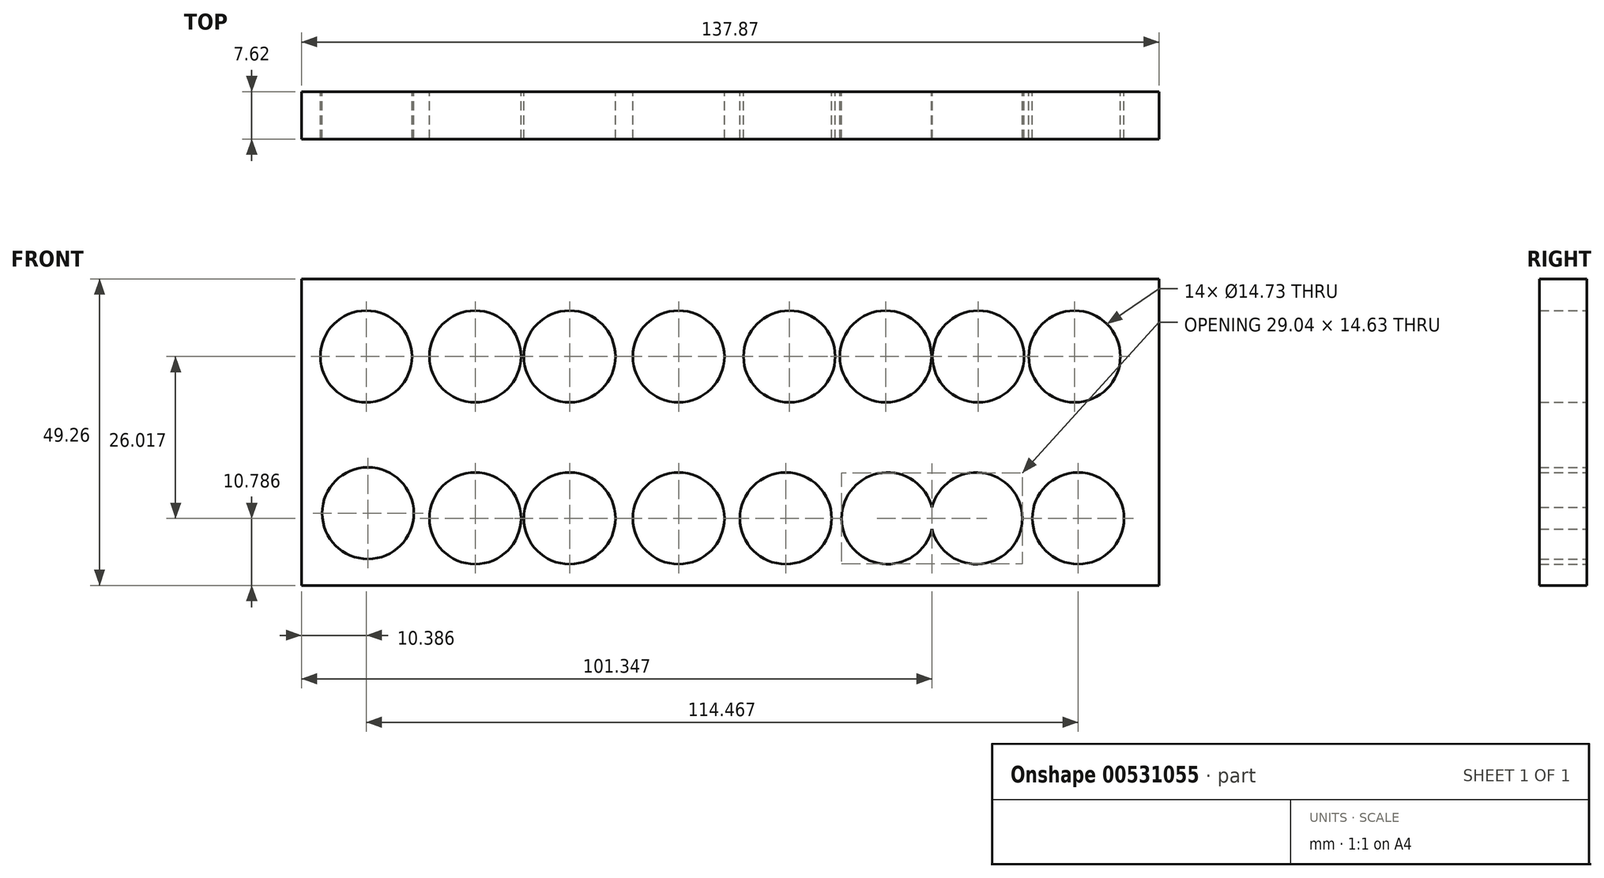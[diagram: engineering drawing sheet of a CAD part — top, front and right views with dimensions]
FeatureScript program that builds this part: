
annotation { "Feature Type Name" : "Feature", "Feature Type Description" : "" }
export const myFeature = defineFeature(function(context is Context, id is Id, definition is map)
    precondition{}
    {
        {
            var Q0;
            Q0=qCreatedBy(makeId("Front.planeOp"),FACE);
            var sketch = newSketch(context, id + "F0", { "sketchPlane" : qUnion([Q0])});
            skLineSegment(sketch, "E0.bottom", {"start": v(-69.08, 21.13) * mm, "end": v(68.79, 21.13) * mm});
            skLineSegment(sketch, "E0.top", {"start": v(-69.08, -28.13) * mm, "end": v(68.79, -28.13) * mm});
            skLineSegment(sketch, "E0.left", {"start": v(-69.08, 21.13) * mm, "end": v(-69.08, -28.13) * mm});
            skLineSegment(sketch, "E0.right", {"start": v(68.79, 21.13) * mm, "end": v(68.79, -28.13) * mm});
            skSolve(sketch);
        }
        {
            var Q0;
            Q0=makeQuery(id+"F0.imprint","IMPRINT",FACE,{"disambiguationData":[TD([[makeQuery(id+"F0.imprint","IMPRINT",EDGE,{"derivedFrom":sQuery(id+"F0.wireOp",EDGE,"E0.bottom")}),-1.0]])]});
            extrude(context, id + "F1", {"entities" : qUnion([Q0]), "depth" : 7.62 * mm, "offsetDistance" : 25.4 * mm});
        }
        {
            var Q0;
            Q0=makeQuery(id+"F1.opExtrude","CAP_FACE",FACE,{"disambiguationData":[OSD([sQuery(id+"F0.wireOp",EDGE,"E0.bottom"),sQuery(id+"F0.wireOp",EDGE,"E0.top"),sQuery(id+"F0.wireOp",EDGE,"E0.left"),sQuery(id+"F0.wireOp",EDGE,"E0.right")])],"isStart":true});
            var sketch = newSketch(context, id + "F2", { "sketchPlane" : qUnion([Q0])});
            skPoint(sketch, "E1", {"position": v(58.4, -16.52) * mm});
            skPoint(sketch, "E2", {"position": v(58.7, 8.67) * mm});
            skPoint(sketch, "E3", {"position": v(41.17, -17.34) * mm});
            skPoint(sketch, "E4", {"position": v(41.17, 8.67) * mm});
            skPoint(sketch, "E5", {"position": v(25.99, -17.34) * mm});
            skPoint(sketch, "E6", {"position": v(25.99, 8.67) * mm});
            skPoint(sketch, "E7", {"position": v(8.47, -17.34) * mm});
            skPoint(sketch, "E8", {"position": v(8.47, 8.67) * mm});
            skPoint(sketch, "E9", {"position": v(-8.76, -17.34) * mm});
            skPoint(sketch, "E10", {"position": v(-9.34, 8.67) * mm});
            skPoint(sketch, "E11", {"position": v(-25.11, -17.34) * mm});
            skPoint(sketch, "E12", {"position": v(-24.82, 8.67) * mm});
            skPoint(sketch, "E13", {"position": v(-39.42, -17.34) * mm});
            skPoint(sketch, "E14", {"position": v(-39.71, 8.67) * mm});
            skPoint(sketch, "E15", {"position": v(-55.77, -17.34) * mm});
            skPoint(sketch, "E16", {"position": v(-55.19, 8.67) * mm});
            skSolve(sketch);
        }
        {
            var Q0;
            Q0=sQuery(id+"F2.wireOp",VERTEX,"E1");
            var Q1;
            Q1=sQuery(id+"F2.wireOp",VERTEX,"E2");
            var Q2;
            Q2=sQuery(id+"F2.wireOp",VERTEX,"E3");
            var Q3;
            Q3=sQuery(id+"F2.wireOp",VERTEX,"E4");
            var Q4;
            Q4=sQuery(id+"F2.wireOp",VERTEX,"E5");
            var Q5;
            Q5=sQuery(id+"F2.wireOp",VERTEX,"E6");
            var Q6;
            Q6=sQuery(id+"F2.wireOp",VERTEX,"E7");
            var Q7;
            Q7=sQuery(id+"F2.wireOp",VERTEX,"E8");
            var Q8;
            Q8=sQuery(id+"F2.wireOp",VERTEX,"E9");
            var Q9;
            Q9=sQuery(id+"F2.wireOp",VERTEX,"E10");
            var Q10;
            Q10=sQuery(id+"F2.wireOp",VERTEX,"E11");
            var Q11;
            Q11=sQuery(id+"F2.wireOp",VERTEX,"E12");
            var Q12;
            Q12=sQuery(id+"F2.wireOp",VERTEX,"E13");
            var Q13;
            Q13=sQuery(id+"F2.wireOp",VERTEX,"E14");
            var Q14;
            Q14=sQuery(id+"F2.wireOp",VERTEX,"E15");
            var Q15;
            Q15=sQuery(id+"F2.wireOp",VERTEX,"E16");
            var Q16;
            Q16=makeQuery(id+"F1.opExtrude","SWEPT_BODY",BODY,{"disambiguationData":[OSD([sQuery(id+"F0.wireOp",EDGE,"E0.bottom"),sQuery(id+"F0.wireOp",EDGE,"E0.top"),sQuery(id+"F0.wireOp",EDGE,"E0.left"),sQuery(id+"F0.wireOp",EDGE,"E0.right")])]});
            hole(context, id + "F3", {"style" : HoleStyle.SIMPLE, "endStyle" : HoleEndStyle.THROUGH, "holeDiameter" : 14.73 * mm, "isTappedThrough" : true, "tappedDepth" : 12.7 * mm, "tapClearance" : 3, "locations" : qUnion([Q0, Q1, Q2, Q3, Q4, Q5, Q6, Q7, Q8, Q9, Q10, Q11, Q12, Q13, Q14, Q15]), "scope" : qUnion([Q16])});
        }
    });
